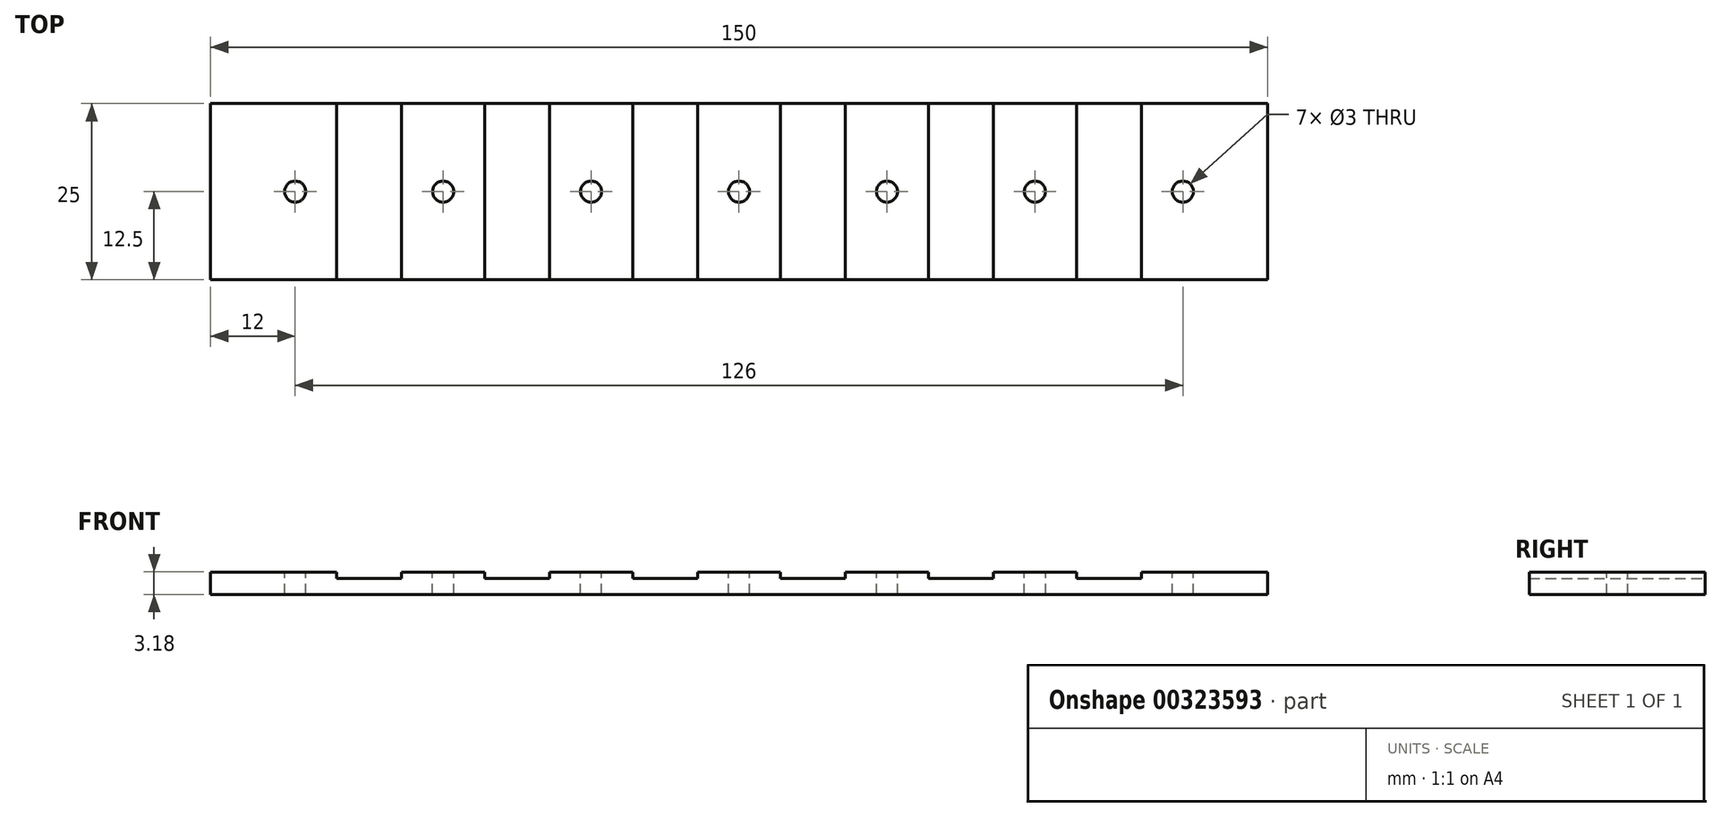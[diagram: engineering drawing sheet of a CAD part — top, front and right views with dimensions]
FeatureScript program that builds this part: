
annotation { "Feature Type Name" : "Feature", "Feature Type Description" : "" }
export const myFeature = defineFeature(function(context is Context, id is Id, definition is map)
    precondition{}
    {
        {
            var Q0;
            Q0=qCreatedBy(makeId("Top.planeOp"),FACE);
            var sketch = newSketch(context, id + "F0", { "sketchPlane" : qUnion([Q0])});
            skLineSegment(sketch, "E0.bottom", {"start": v(0, 0) * mm, "end": v(150, 0) * mm});
            skLineSegment(sketch, "E0.top", {"start": v(0, 25) * mm, "end": v(150, 25) * mm});
            skLineSegment(sketch, "E0.left", {"start": v(0, 0) * mm, "end": v(0, 25) * mm});
            skLineSegment(sketch, "E0.right", {"start": v(150, 0) * mm, "end": v(150, 25) * mm});
            skSolve(sketch);
        }
        {
            var Q0;
            Q0 = qSketchRegion(id + "F0", true);
            extrude(context, id + "F1", {"entities" : qUnion([Q0]), "depth" : 3.17 * mm});
        }
        {
            var Q0;
            Q0=makeQuery(id+"F1.opExtrude","CAP_FACE",FACE,{"disambiguationData":[OSD([sQuery(id+"F0.wireOp",EDGE,"E0.bottom"),sQuery(id+"F0.wireOp",EDGE,"E0.top"),sQuery(id+"F0.wireOp",EDGE,"E0.left"),sQuery(id+"F0.wireOp",EDGE,"E0.right")])],"isStart":false});
            var sketch = newSketch(context, id + "F2", { "sketchPlane" : qUnion([Q0])});
            skLineSegment(sketch, "E1.bottom", {"start": v(17.9, 0) * mm, "end": v(27.1, 0) * mm});
            skLineSegment(sketch, "E1.top", {"start": v(17.9, 25) * mm, "end": v(27.1, 25) * mm});
            skLineSegment(sketch, "E1.left", {"start": v(17.9, 0) * mm, "end": v(17.9, 25) * mm});
            skLineSegment(sketch, "E1.right", {"start": v(27.1, 0) * mm, "end": v(27.1, 25) * mm});
            skLineSegment(sketch, "E2.1.0.0", {"start": v(48.1, 0) * mm, "end": v(48.1, 25) * mm});
            skLineSegment(sketch, "E2.1.0.1", {"start": v(38.9, 0) * mm, "end": v(38.9, 25) * mm});
            skLineSegment(sketch, "E2.1.0.2", {"start": v(38.9, 25) * mm, "end": v(48.1, 25) * mm});
            skLineSegment(sketch, "E2.1.0.3", {"start": v(38.9, 0) * mm, "end": v(48.1, 0) * mm});
            skLineSegment(sketch, "E2.2.0.0", {"start": v(69.1, 0) * mm, "end": v(69.1, 25) * mm});
            skLineSegment(sketch, "E2.2.0.1", {"start": v(59.9, 0) * mm, "end": v(59.9, 25) * mm});
            skLineSegment(sketch, "E2.2.0.2", {"start": v(59.9, 25) * mm, "end": v(69.1, 25) * mm});
            skLineSegment(sketch, "E2.2.0.3", {"start": v(59.9, 0) * mm, "end": v(69.1, 0) * mm});
            skLineSegment(sketch, "E2.3.0.0", {"start": v(90.1, 0) * mm, "end": v(90.1, 25) * mm});
            skLineSegment(sketch, "E2.3.0.1", {"start": v(80.9, 0) * mm, "end": v(80.9, 25) * mm});
            skLineSegment(sketch, "E2.3.0.2", {"start": v(80.9, 25) * mm, "end": v(90.1, 25) * mm});
            skLineSegment(sketch, "E2.3.0.3", {"start": v(80.9, 0) * mm, "end": v(90.1, 0) * mm});
            skLineSegment(sketch, "E2.4.0.0", {"start": v(111.1, 0) * mm, "end": v(111.1, 25) * mm});
            skLineSegment(sketch, "E2.4.0.1", {"start": v(101.9, 0) * mm, "end": v(101.9, 25) * mm});
            skLineSegment(sketch, "E2.4.0.2", {"start": v(101.9, 25) * mm, "end": v(111.1, 25) * mm});
            skLineSegment(sketch, "E2.4.0.3", {"start": v(101.9, 0) * mm, "end": v(111.1, 0) * mm});
            skLineSegment(sketch, "E2.5.0.0", {"start": v(132.1, 0) * mm, "end": v(132.1, 25) * mm});
            skLineSegment(sketch, "E2.5.0.1", {"start": v(122.9, 0) * mm, "end": v(122.9, 25) * mm});
            skLineSegment(sketch, "E2.5.0.2", {"start": v(122.9, 25) * mm, "end": v(132.1, 25) * mm});
            skLineSegment(sketch, "E2.5.0.3", {"start": v(122.9, 0) * mm, "end": v(132.1, 0) * mm});
            skLineSegment(sketch, "E2.direction1", {"start": v(17.9, 0) * mm, "end": v(38.9, 0) * mm, "construction": true});
            skSolve(sketch);
        }
        {
            var Q0;
            Q0 = qSketchRegion(id + "F2", true);
            extrude(context, id + "F3", {"entities" : qUnion([Q0]), "operationType" : NewBodyOperationType.REMOVE, "oppositeDirection" : true, "depth" : .9 * mm});
        }
        {
            var Q0;
            Q0=makeQuery(id+"F1.opExtrude","CAP_FACE",FACE,{"disambiguationData":[OSD([sQuery(id+"F0.wireOp",EDGE,"E0.bottom"),sQuery(id+"F0.wireOp",EDGE,"E0.top"),sQuery(id+"F0.wireOp",EDGE,"E0.left"),sQuery(id+"F0.wireOp",EDGE,"E0.right")])],"isStart":false});
            var sketch = newSketch(context, id + "F4", { "sketchPlane" : qUnion([Q0])});
            skCircle(sketch, "E3", {"center": v(12, 12.5) * mm, "radius": 1.5 * mm});
            skCircle(sketch, "E4.1.0.0", {"center": v(33, 12.5) * mm, "radius": 1.5 * mm});
            skCircle(sketch, "E4.2.0.0", {"center": v(54, 12.5) * mm, "radius": 1.5 * mm});
            skCircle(sketch, "E4.3.0.0", {"center": v(75, 12.5) * mm, "radius": 1.5 * mm});
            skCircle(sketch, "E4.4.0.0", {"center": v(96, 12.5) * mm, "radius": 1.5 * mm});
            skCircle(sketch, "E4.5.0.0", {"center": v(117, 12.5) * mm, "radius": 1.5 * mm});
            skCircle(sketch, "E4.6.0.0", {"center": v(138, 12.5) * mm, "radius": 1.5 * mm});
            skLineSegment(sketch, "E4.direction1", {"start": v(12, 12.5) * mm, "end": v(33, 12.5) * mm, "construction": true});
            skSolve(sketch);
        }
        {
            var Q0;
            Q0 = qSketchRegion(id + "F4", true);
            extrude(context, id + "F5", {"entities" : qUnion([Q0]), "operationType" : NewBodyOperationType.REMOVE, "oppositeDirection" : true, "depth" : 25 * mm});
        }
    });
